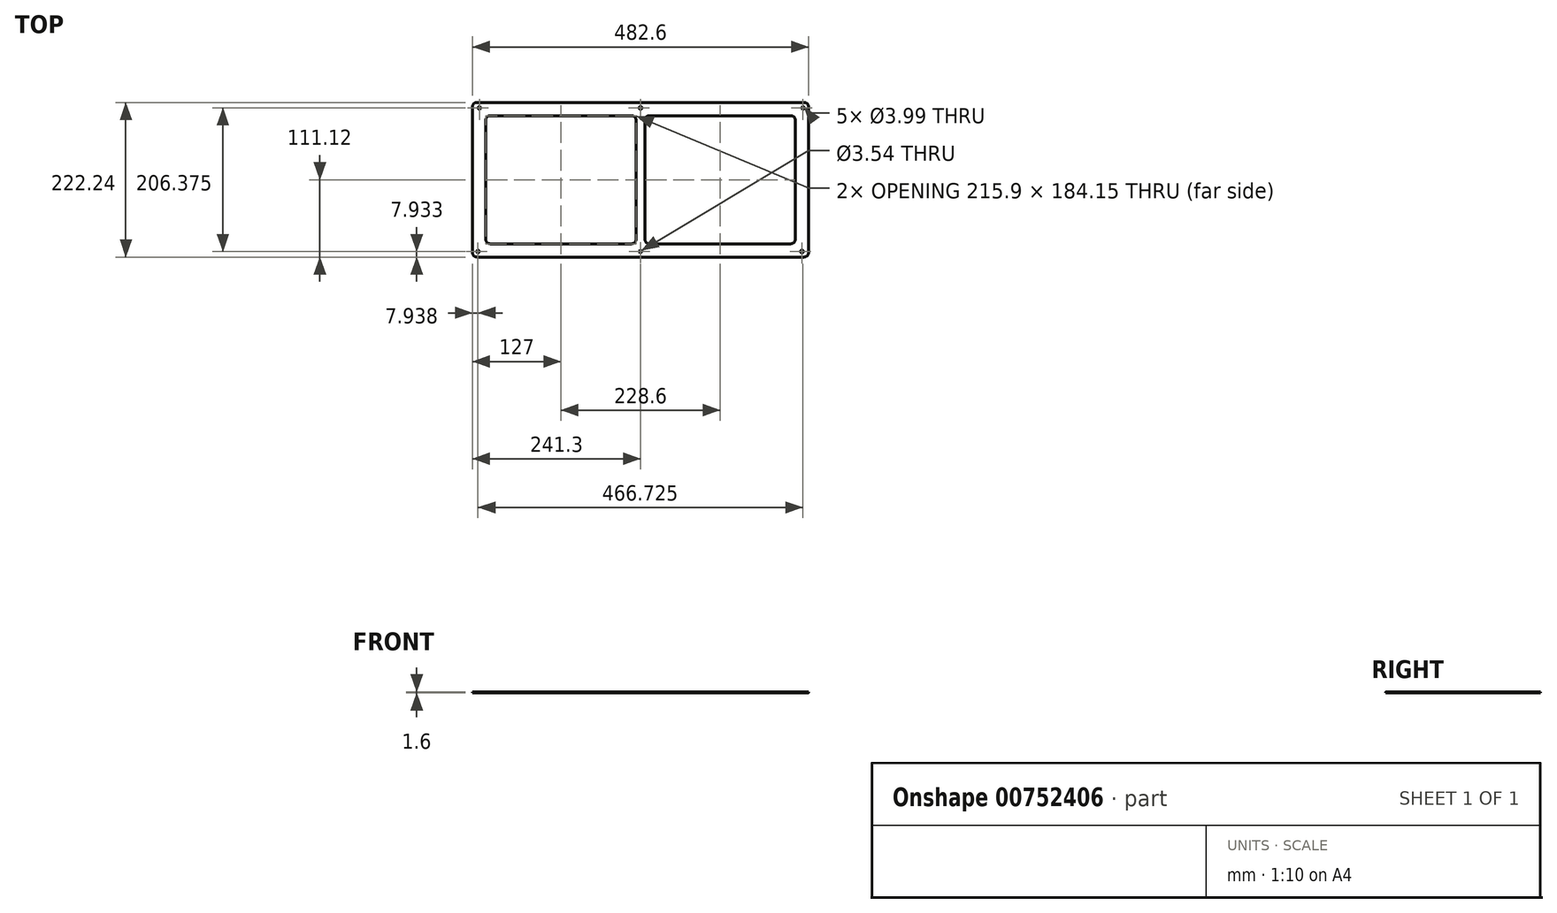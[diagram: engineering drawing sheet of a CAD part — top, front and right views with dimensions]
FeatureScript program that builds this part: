
annotation { "Feature Type Name" : "Feature", "Feature Type Description" : "" }
export const myFeature = defineFeature(function(context is Context, id is Id, definition is map)
    precondition{}
    {
        {
            var Q0;
            Q0=qCreatedBy(makeId("Top.planeOp"),FACE);
            var sketch = newSketch(context, id + "F0", { "sketchPlane" : qUnion([Q0])});
            skLineSegment(sketch, "E0.bottom", {"start": v(-234.95, -111.13) * mm, "end": v(234.95, -111.13) * mm});
            skLineSegment(sketch, "E0.top", {"start": v(-234.95, 111.13) * mm, "end": v(234.95, 111.13) * mm});
            skLineSegment(sketch, "E0.left", {"start": v(-241.3, -104.78) * mm, "end": v(-241.3, 104.78) * mm});
            skLineSegment(sketch, "E0.right", {"start": v(241.3, -104.78) * mm, "end": v(241.3, 104.78) * mm});
            skPoint(sketch, "E0.middle", {"position": v(0, 0) * mm});
            skPoint(sketch, "E1.visualSharp", {"position": v(-241.3, 111.13) * mm});
            skArc(sketch, "E1.filletArc", {"start": v(-234.95, 111.13) * mm, "mid": v(-239.44, 109.27) * mm, "end": v(-241.3, 104.78) * mm});
            skPoint(sketch, "E2.visualSharp", {"position": v(-241.3, -111.13) * mm});
            skArc(sketch, "E2.filletArc", {"start": v(-241.3, -104.78) * mm, "mid": v(-239.44, -109.27) * mm, "end": v(-234.95, -111.13) * mm});
            skPoint(sketch, "E3.visualSharp", {"position": v(241.3, -111.13) * mm});
            skArc(sketch, "E3.filletArc", {"start": v(234.95, -111.13) * mm, "mid": v(239.44, -109.27) * mm, "end": v(241.3, -104.78) * mm});
            skPoint(sketch, "E4.visualSharp", {"position": v(241.3, 111.13) * mm});
            skArc(sketch, "E4.filletArc", {"start": v(241.3, 104.78) * mm, "mid": v(239.44, 109.27) * mm, "end": v(234.95, 111.13) * mm});
            skSolve(sketch);
        }
        {
            var Q0;
            Q0 = qSketchRegion(id + "F0", true);
            extrude(context, id + "F1", {"entities" : qUnion([Q0]), "oppositeDirection" : true, "depth" : 1.6 * mm, "offsetDistance" : 25.4 * mm});
        }
        {
            var Q0;
            Q0=makeQuery(id+"F1.opExtrude","CAP_FACE",FACE,{"disambiguationData":[OSD([sQuery(id+"F0.wireOp",EDGE,"E0.bottom"),sQuery(id+"F0.wireOp",EDGE,"E0.top"),sQuery(id+"F0.wireOp",EDGE,"E0.left"),sQuery(id+"F0.wireOp",EDGE,"E0.right")])],"isStart":true});
            var sketch = newSketch(context, id + "F2", { "sketchPlane" : qUnion([Q0])});
            skLineSegment(sketch, "E5.bottom", {"start": v(-215.9, -92.08) * mm, "end": v(-12.7, -92.08) * mm});
            skLineSegment(sketch, "E5.top", {"start": v(-215.9, 92.08) * mm, "end": v(-12.7, 92.08) * mm});
            skLineSegment(sketch, "E5.left", {"start": v(-222.25, -85.73) * mm, "end": v(-222.25, 85.73) * mm});
            skLineSegment(sketch, "E5.right", {"start": v(222.25, -85.73) * mm, "end": v(222.25, 85.73) * mm});
            skPoint(sketch, "E5.middle", {"position": v(0, 0) * mm});
            skLineSegment(sketch, "E6.0", {"start": v(-6.35, 85.73) * mm, "end": v(-6.35, -85.73) * mm});
            skLineSegment(sketch, "E7.0", {"start": v(6.35, 85.73) * mm, "end": v(6.35, -85.73) * mm});
            skPoint(sketch, "E8.orphan", {"position": v(0, 92.08) * mm});
            skLineSegment(sketch, "E9.trimOffspring", {"start": v(12.7, 92.08) * mm, "end": v(215.9, 92.08) * mm});
            skPoint(sketch, "E10.end.orphan", {"position": v(0, -92.08) * mm});
            skLineSegment(sketch, "E11.trimOffspring", {"start": v(12.7, -92.08) * mm, "end": v(215.9, -92.08) * mm});
            skPoint(sketch, "E12.visualSharp", {"position": v(222.25, 92.08) * mm});
            skArc(sketch, "E12.filletArc", {"start": v(222.25, 85.73) * mm, "mid": v(220.4, 90.22) * mm, "end": v(215.9, 92.08) * mm});
            skPoint(sketch, "E13.visualSharp", {"position": v(6.35, 92.08) * mm});
            skArc(sketch, "E13.filletArc", {"start": v(12.7, 92.08) * mm, "mid": v(8.2, 90.22) * mm, "end": v(6.35, 85.73) * mm});
            skPoint(sketch, "E14.visualSharp", {"position": v(-6.35, 92.08) * mm});
            skArc(sketch, "E14.filletArc", {"start": v(-6.35, 85.73) * mm, "mid": v(-8.2, 90.22) * mm, "end": v(-12.7, 92.08) * mm});
            skPoint(sketch, "E15.visualSharp", {"position": v(-222.25, 92.08) * mm});
            skArc(sketch, "E15.filletArc", {"start": v(-215.9, 92.08) * mm, "mid": v(-220.4, 90.22) * mm, "end": v(-222.25, 85.73) * mm});
            skPoint(sketch, "E16.visualSharp", {"position": v(-222.25, -92.08) * mm});
            skArc(sketch, "E16.filletArc", {"start": v(-222.25, -85.73) * mm, "mid": v(-220.4, -90.22) * mm, "end": v(-215.9, -92.08) * mm});
            skPoint(sketch, "E17.visualSharp", {"position": v(-6.35, -92.08) * mm});
            skArc(sketch, "E17.filletArc", {"start": v(-12.7, -92.08) * mm, "mid": v(-8.2, -90.22) * mm, "end": v(-6.35, -85.73) * mm});
            skPoint(sketch, "E18.visualSharp", {"position": v(6.35, -92.08) * mm});
            skArc(sketch, "E18.filletArc", {"start": v(6.35, -85.73) * mm, "mid": v(8.2, -90.22) * mm, "end": v(12.7, -92.08) * mm});
            skPoint(sketch, "E19.visualSharp", {"position": v(222.25, -92.08) * mm});
            skArc(sketch, "E19.filletArc", {"start": v(215.9, -92.08) * mm, "mid": v(220.4, -90.22) * mm, "end": v(222.25, -85.73) * mm});
            skSolve(sketch);
        }
        {
            var Q0;
            Q0 = qSketchRegion(id + "F2", true);
            extrude(context, id + "F3", {"entities" : qUnion([Q0]), "operationType" : NewBodyOperationType.REMOVE, "endBound" : BoundingType.THROUGH_ALL, "oppositeDirection" : true, "depth" : 25.4 * mm, "offsetDistance" : 25.4 * mm});
        }
        {
            var Q0;
            Q0=makeQuery(id+"F1.opExtrude","CAP_FACE",FACE,{"disambiguationData":[OSD([sQuery(id+"F0.wireOp",EDGE,"E0.bottom"),sQuery(id+"F0.wireOp",EDGE,"E0.top"),sQuery(id+"F0.wireOp",EDGE,"E0.left"),sQuery(id+"F0.wireOp",EDGE,"E0.right")])],"isStart":true});
            var sketch = newSketch(context, id + "F4", { "sketchPlane" : qUnion([Q0])});
            skCircle(sketch, "E20", {"center": v(-231.37, 103.19) * mm, "radius": 2 * mm});
            skCircle(sketch, "E21", {"center": v(0, -103.19) * mm, "radius": 1.77 * mm});
            skPoint(sketch, "E21.centerSnap0", {"position": v(0, -111.13) * mm});
            skCircle(sketch, "E22", {"center": v(0, 103.19) * mm, "radius": 2 * mm});
            skCircle(sketch, "E23", {"center": v(233.36, 103.19) * mm, "radius": 2 * mm});
            skCircle(sketch, "E24", {"center": v(231.82, -103.19) * mm, "radius": 2 * mm});
            skPoint(sketch, "E25.center.orphan", {"position": v(-233.36, -103.19) * mm});
            skCircle(sketch, "E26", {"center": v(-233.36, -103.19) * mm, "radius": 2 * mm});
            skSolve(sketch);
        }
        {
            var Q0;
            Q0 = qSketchRegion(id + "F4", true);
            extrude(context, id + "F5", {"entities" : qUnion([Q0]), "operationType" : NewBodyOperationType.REMOVE, "endBound" : BoundingType.THROUGH_ALL, "oppositeDirection" : true, "depth" : 25.4 * mm, "offsetDistance" : 25.4 * mm});
        }
    });
